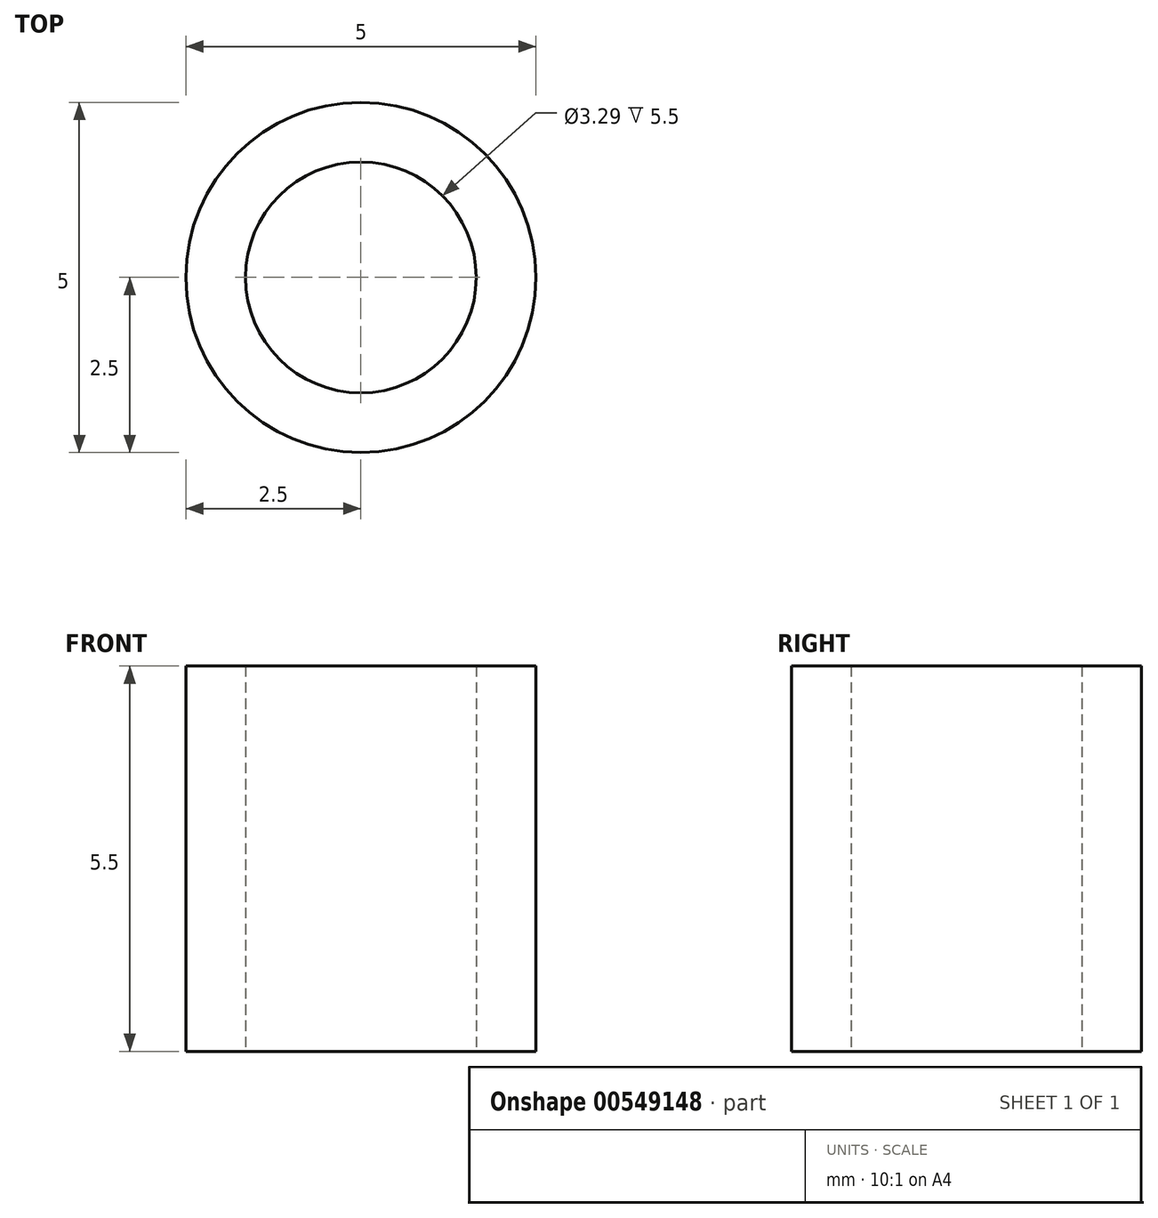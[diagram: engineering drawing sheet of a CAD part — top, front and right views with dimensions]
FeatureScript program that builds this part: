
annotation { "Feature Type Name" : "Feature", "Feature Type Description" : "" }
export const myFeature = defineFeature(function(context is Context, id is Id, definition is map)
    precondition{}
    {
        {
            var Q0;
            Q0=qCreatedBy(makeId("Top.planeOp"),FACE);
            var sketch = newSketch(context, id + "F0", { "sketchPlane" : qUnion([Q0])});
            skCircle(sketch, "E0", {"center": v(0, 0) * mm, "radius": 2.5 * mm});
            skCircle(sketch, "E1", {"center": v(0, 0) * mm, "radius": 1.65 * mm});
            skSolve(sketch);
        }
        {
            var Q0;
            Q0=makeQuery(id+"F0.imprint","IMPRINT",FACE,{"disambiguationData":[TD([[makeQuery(id+"F0.imprint","IMPRINT",EDGE,{"derivedFrom":sQuery(id+"F0.wireOp",EDGE,"E0")}),1.0]])]});
            extrude(context, id + "F1", {"entities" : qUnion([Q0]), "depth" : 5.5 * mm, "offsetDistance" : 25.4 * mm});
        }
    });
